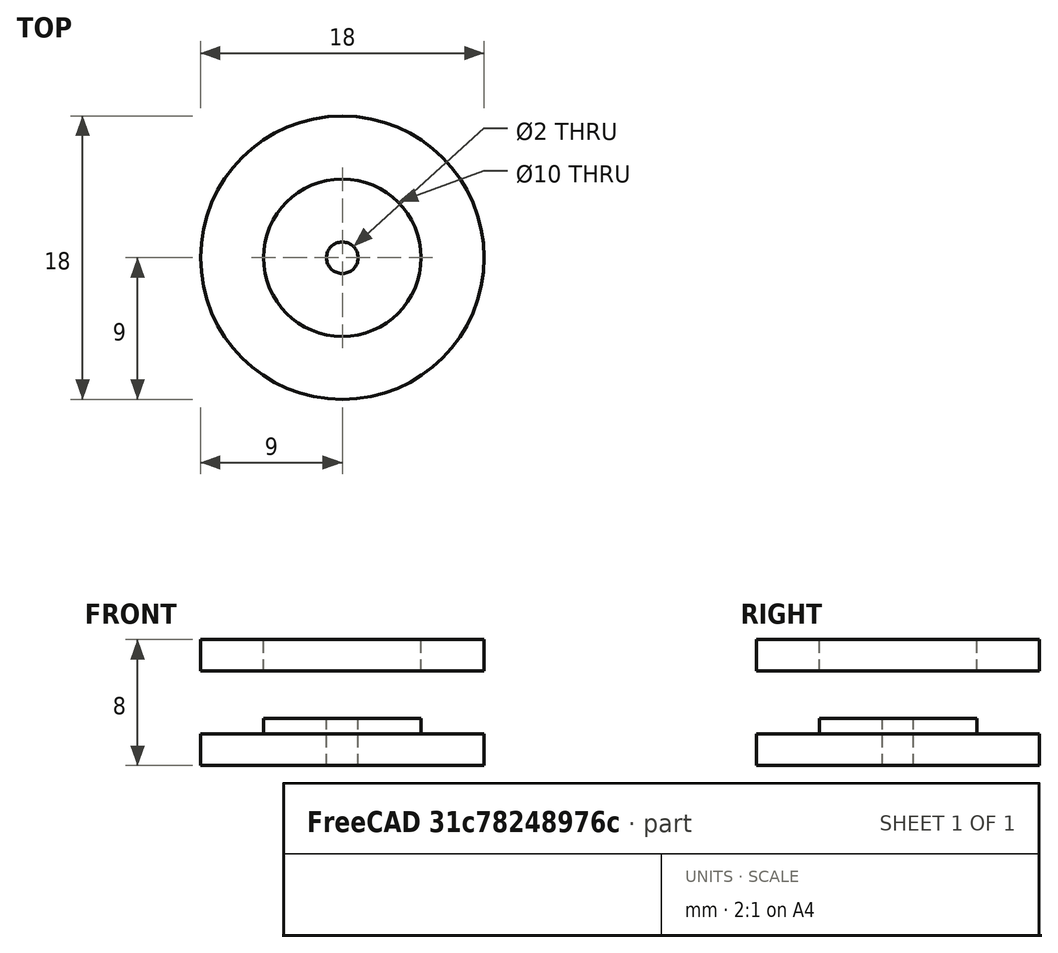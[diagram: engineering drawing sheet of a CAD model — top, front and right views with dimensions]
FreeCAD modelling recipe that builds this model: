
FCSTD DOCUMENT  (FreeCAD 0.15R4671 (Git))
Label: catherine-wheel-hub
License: All rights reserved
LicenseURL: http://en.wikipedia.org/wiki/All_rights_reserved
objects: Part::Cylinder×5, Part::Cut×2, Part::Fuse×1
note: 8 computed .brp shape members not serialized (recipe doc carries the construction recipe); baked Part::Feature solids carry a one-line shape summary decoded from their .brp

FEATURE [Part::Cylinder] Cylinder
  Angle = 360
  Height = 3
  Radius = 5
FEATURE [Part::Cylinder] Cylinder001
  Angle = 360
  Height = 2
  Radius = 9
FEATURE [Part::Cylinder] Cylinder002
  Angle = 360
  Height = 11
  Placement = pos=(0,0,-3) rot=(0,0,1;0rad)
  Radius = 1
FEATURE [Part::Cylinder] Cylinder003
  Angle = 360
  Height = 2
  Radius = 9
FEATURE [Part::Cylinder] Cylinder004
  Angle = 360
  Height = 4
  Placement = pos=(0,0,-1) rot=(0,0,1;0rad)
  Radius = 5
FEATURE [Part::Fuse] Fusion
  Base = -> Cylinder
  Tool = -> Cylinder001
FEATURE [Part::Cut] Cut
  Base = -> Fusion
  Placement = pos=(0,0,-6) rot=(0,0,1;0rad)
  Tool = -> Cylinder002
FEATURE [Part::Cut] Cut001
  Base = -> Cylinder003
  Tool = -> Cylinder004
